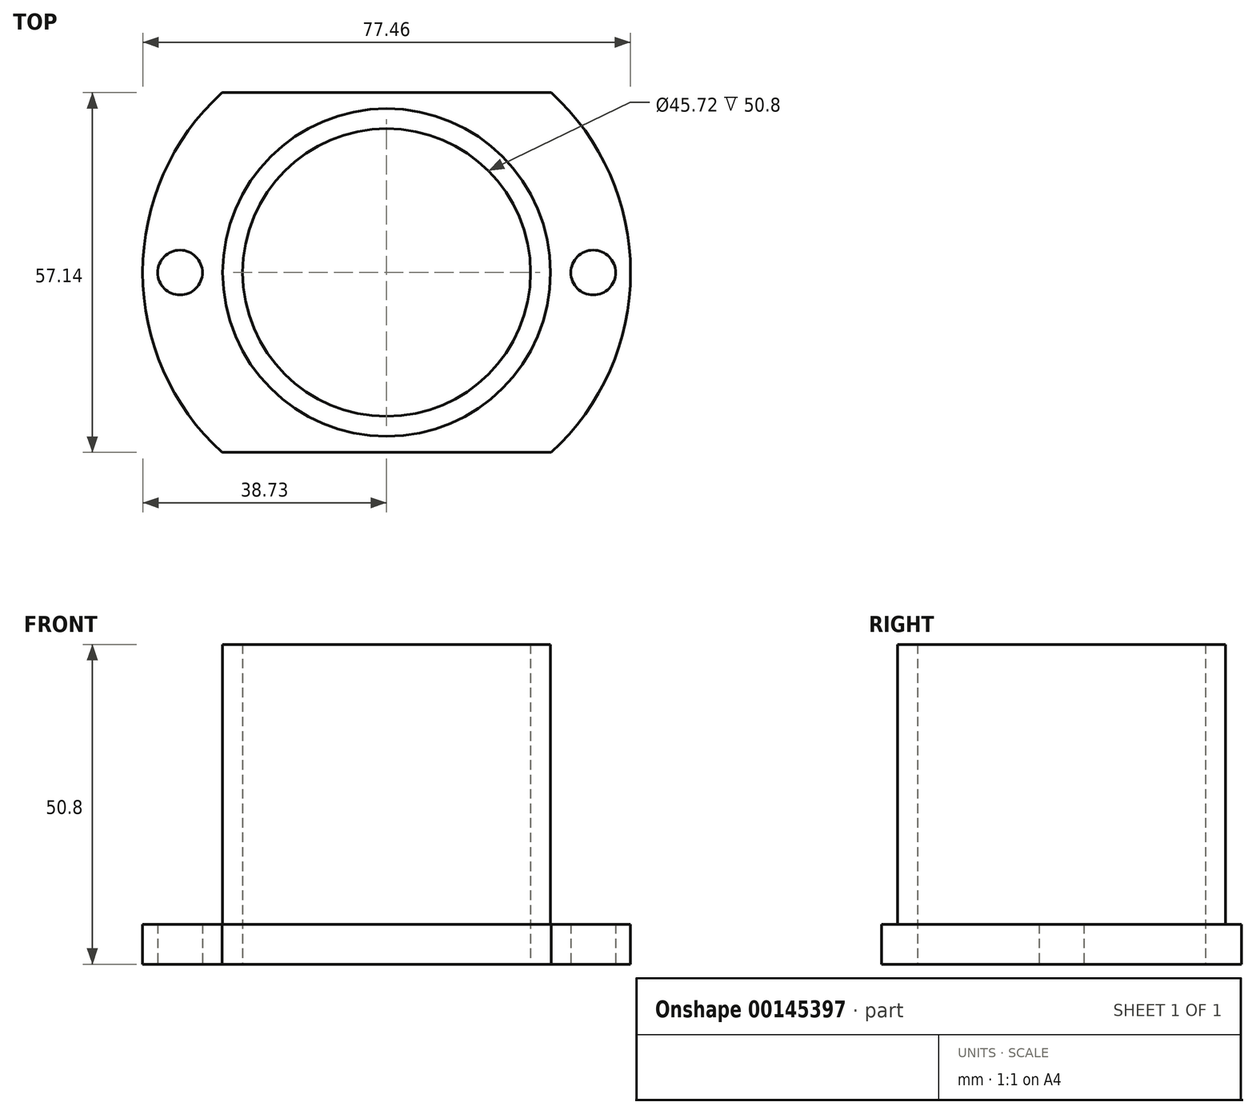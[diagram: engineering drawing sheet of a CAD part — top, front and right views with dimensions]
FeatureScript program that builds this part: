
annotation { "Feature Type Name" : "Feature", "Feature Type Description" : "" }
export const myFeature = defineFeature(function(context is Context, id is Id, definition is map)
    precondition{}
    {
        {
            var Q0;
            Q0=qCreatedBy(makeId("Top.planeOp"),FACE);
            var sketch = newSketch(context, id + "F0", { "sketchPlane" : qUnion([Q0])});
            skCircle(sketch, "E0", {"center": v(0, 0) * mm, "radius": 22.86 * mm});
            skCircle(sketch, "E1.0", {"center": v(0, 0) * mm, "radius": 26.04 * mm});
            skArc(sketch, "E2.0", {"start": v(-26.15, 28.57) * mm, "mid": v(-38.74, 0) * mm, "end": v(-26.15, -28.58) * mm});
            skCircle(sketch, "E3", {"center": v(32.8, 0) * mm, "radius": 3.56 * mm});
            skCircle(sketch, "E4.MirrorC", {"center": v(-32.8, 0) * mm, "radius": 3.56 * mm});
            skLineSegment(sketch, "E5.bottom", {"start": v(26.15, 28.58) * mm, "end": v(-26.15, 28.58) * mm});
            skLineSegment(sketch, "E5.top", {"start": v(26.15, -28.58) * mm, "end": v(-26.15, -28.58) * mm});
            skArc(sketch, "E6.trimOffspring", {"start": v(26.15, -28.58) * mm, "mid": v(38.74, 0) * mm, "end": v(26.15, 28.57) * mm});
            skPoint(sketch, "E5.right.end.orphan", {"position": v(-50.33, -28.57) * mm});
            skPoint(sketch, "E5.right.start.orphan", {"position": v(-50.33, 28.58) * mm});
            skPoint(sketch, "E7.orphan", {"position": v(50.33, 28.57) * mm});
            skPoint(sketch, "E8.orphan", {"position": v(50.33, -28.58) * mm});
            skSolve(sketch);
        }
        {
            var Q0;
            Q0=makeQuery(id+"F0.imprint","IMPRINT",FACE,{"disambiguationData":[TD([[makeQuery(id+"F0.imprint","IMPRINT",EDGE,{"derivedFrom":sQuery(id+"F0.wireOp",EDGE,"E0")}),-1.0]])]});
            extrude(context, id + "F1", {"entities" : qUnion([Q0]), "depth" : 50.8 * mm});
        }
        {
            var Q0;
            Q0=makeQuery(id+"F0.imprint","IMPRINT",FACE,{"disambiguationData":[TD([[makeQuery(id+"F0.imprint","IMPRINT",EDGE,{"derivedFrom":sQuery(id+"F0.wireOp",EDGE,"E1.0")}),-1.0]])]});
            extrude(context, id + "F2", {"entities" : qUnion([Q0]), "operationType" : NewBodyOperationType.ADD, "depth" : 6.35 * mm});
        }
    });
